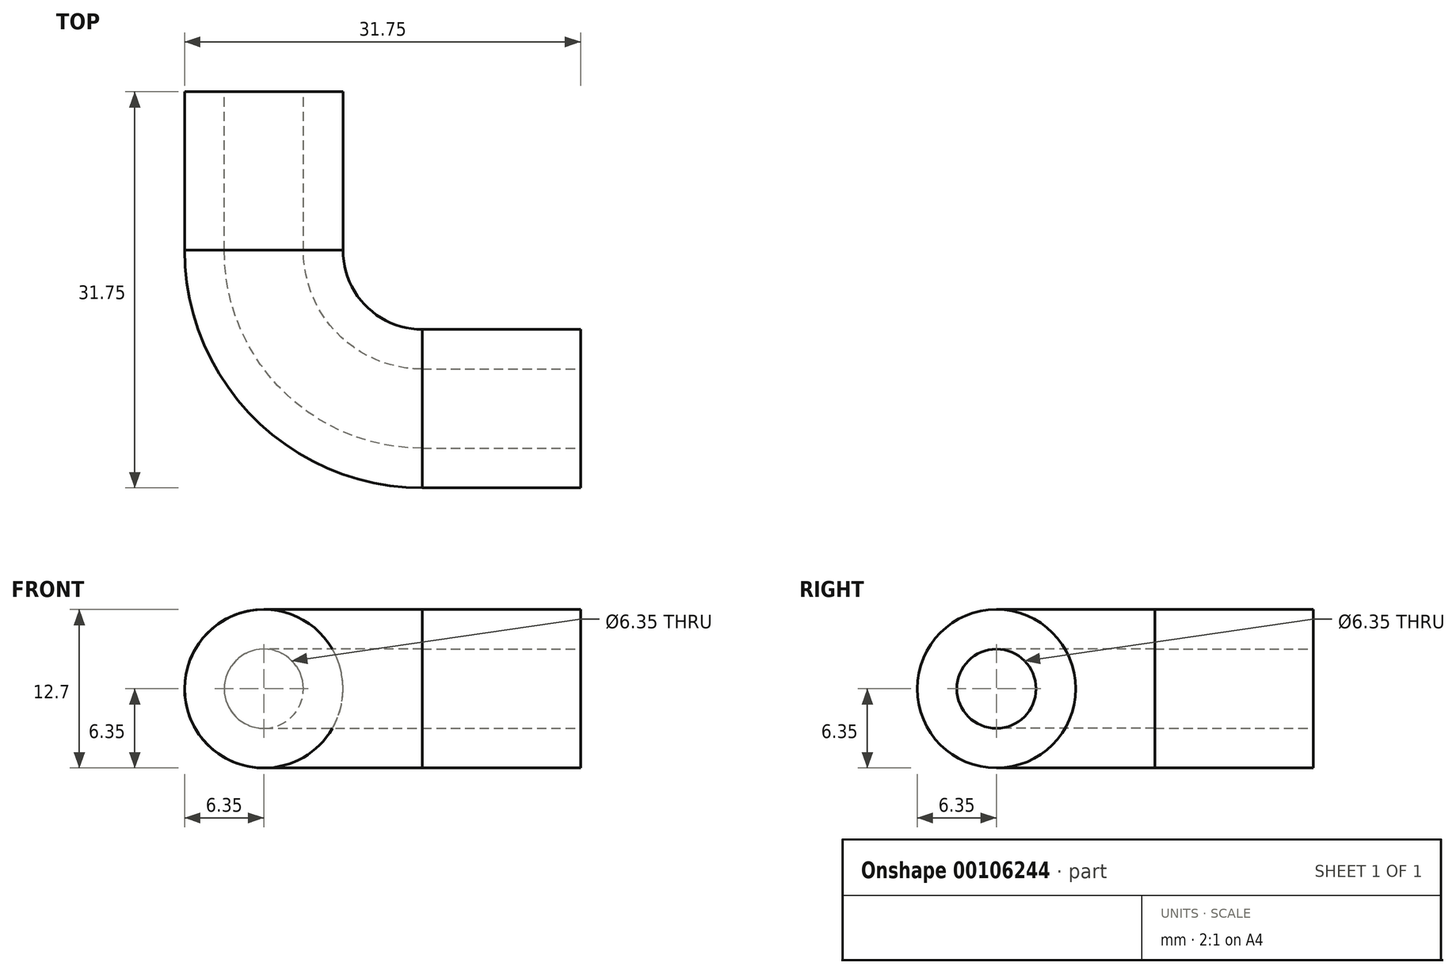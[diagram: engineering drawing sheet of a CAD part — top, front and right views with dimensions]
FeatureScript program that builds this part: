
annotation { "Feature Type Name" : "Feature", "Feature Type Description" : "" }
export const myFeature = defineFeature(function(context is Context, id is Id, definition is map)
    precondition{}
    {
        {
            var Q0;
            Q0=qCreatedBy(makeId("Right.planeOp"),FACE);
            var sketch = newSketch(context, id + "F0", { "sketchPlane" : qUnion([Q0])});
            skCircle(sketch, "E0", {"center": v(-25.4, 0) * mm, "radius": 6.35 * mm});
            skCircle(sketch, "E1", {"center": v(-25.4, 0) * mm, "radius": 3.18 * mm});
            skSolve(sketch);
        }
        {
            var Q0;
            Q0 = qSketchRegion(id + "F0", true);
            extrude(context, id + "F1", {"entities" : qUnion([Q0]), "oppositeDirection" : true, "depth" : 12.7 * mm});
        }
        {
            var Q0;
            Q0=qCreatedBy(makeId("Front.planeOp"),FACE);
            var sketch = newSketch(context, id + "F2", { "sketchPlane" : qUnion([Q0])});
            skCircle(sketch, "E2", {"center": v(-25.4, 0) * mm, "radius": 6.35 * mm});
            skCircle(sketch, "E3", {"center": v(-25.4, 0) * mm, "radius": 3.18 * mm});
            skSolve(sketch);
        }
        {
            var Q0;
            Q0 = qSketchRegion(id + "F2", true);
            extrude(context, id + "F3", {"entities" : qUnion([Q0]), "depth" : 12.7 * mm});
        }
        {
            var Q0;
            Q0=qCreatedBy(makeId("Top.planeOp"),FACE);
            var sketch = newSketch(context, id + "F4", { "sketchPlane" : qUnion([Q0])});
            skLineSegment(sketch, "E4", {"start": v(-12.7, -65.62) * mm, "end": v(-12.7, -12.83) * mm, "construction": true});
            skLineSegment(sketch, "E5", {"start": v(-21.72, -12.7) * mm, "end": v(-68.1, -12.7) * mm, "construction": true});
            skArc(sketch, "E6", {"start": v(-38.1, -12.7) * mm, "mid": v(-30.66, -30.66) * mm, "end": v(-12.7, -38.1) * mm});
            skSolve(sketch);
        }
        {
            var Q0;
            Q0=makeQuery(id+"F3.opExtrude","CAP_FACE",FACE,{"disambiguationData":[OSD([sQuery(id+"F2.wireOp",EDGE,"E2"),sQuery(id+"F2.wireOp",EDGE,"E3")])],"isStart":false});
            var Q1;
            Q1=sQuery(id+"F4.wireOp",EDGE,"E6");
            sweep(context, id + "F5", {"profiles" : qUnion([Q0]), "path" : qUnion([Q1])});
        }
    });
